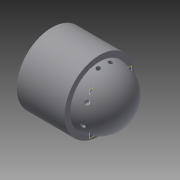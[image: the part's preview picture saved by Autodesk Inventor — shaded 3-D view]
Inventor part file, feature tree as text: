
AUTODESK INVENTOR PART (.ipt)
format: ipt  version: 2014 SP2 (Build 180246200, 246)  size: 171,008 bytes
history: native  units: mm
features: other x3, extrude x1, plane x1, sketch x1
ambient origin geometry x8: Origin, YZ Plane, XZ Plane, XY Plane, X Axis, Y Axis, Z Axis, Center Point
bodies: Solid1 (feature_tree)
feature tree (6):
  other  "pressure-end1.ipt"
  extrude  "Extrusion1"  Depth=15.0mm
  other  "Solid1::pressure-end1.ipt"
  other  "TaggingFeature1"
  plane  "Work Plane1"
  sketch  "Sketch1"  dims[d0=12.3mm d1=22.0mm d2=15.0mm d3=0.0mm]
